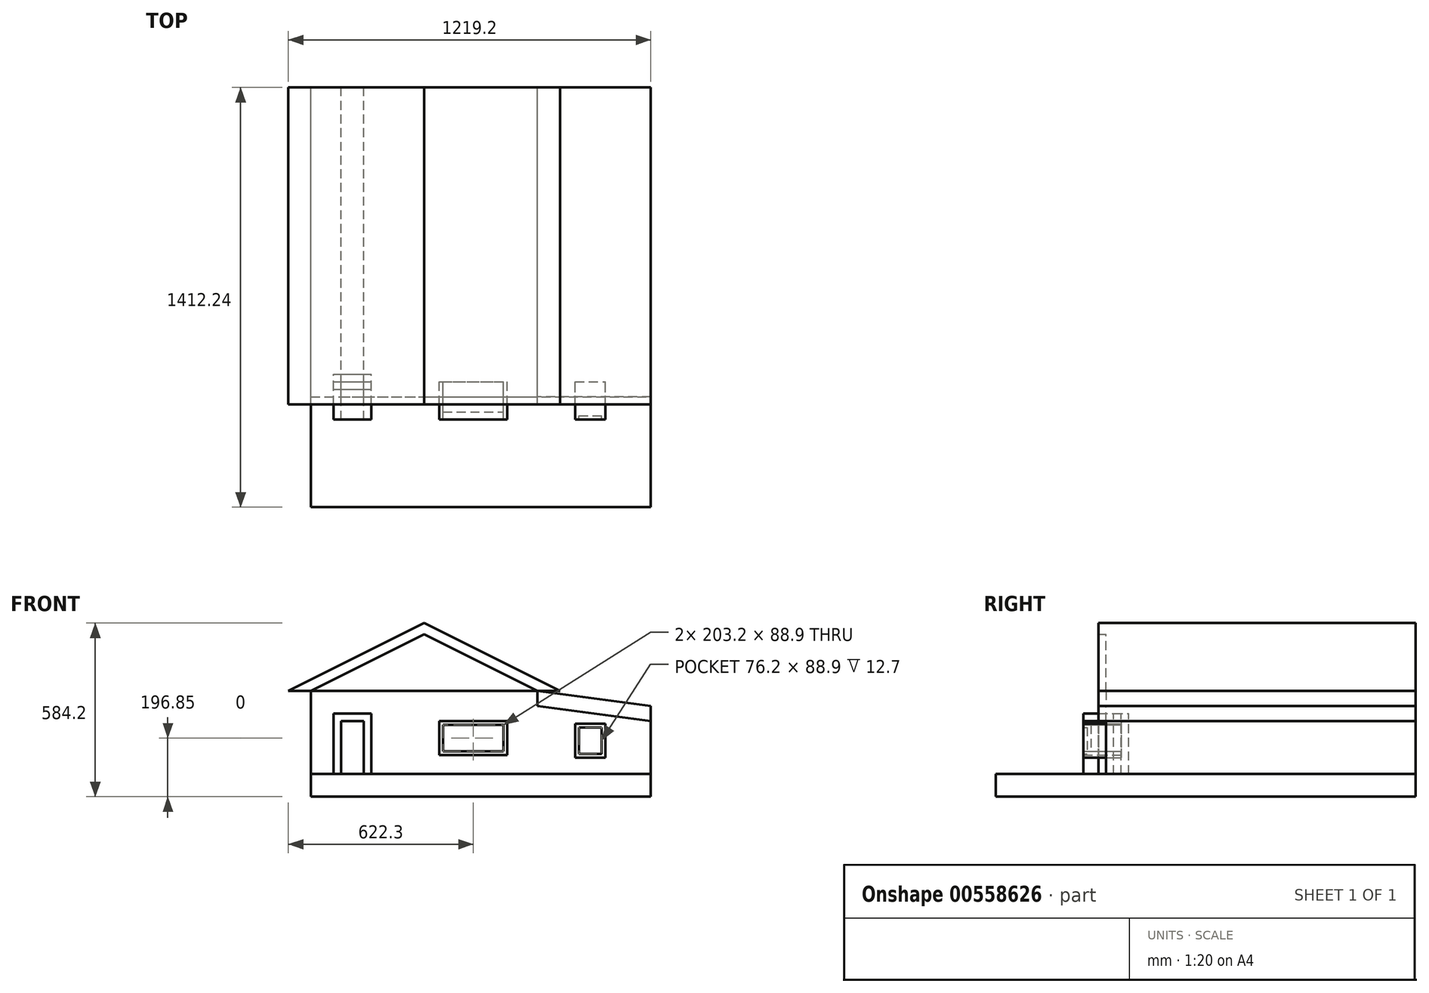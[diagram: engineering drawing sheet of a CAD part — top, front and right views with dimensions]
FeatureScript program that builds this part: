
annotation { "Feature Type Name" : "Feature", "Feature Type Description" : "" }
export const myFeature = defineFeature(function(context is Context, id is Id, definition is map)
    precondition{}
    {
        {
            var Q0;
            Q0=qCreatedBy(makeId("Front.planeOp"),FACE);
            var sketch = newSketch(context, id + "F0", { "sketchPlane" : qUnion([Q0])});
            skLineSegment(sketch, "E0", {"start": v(0, 0) * mm, "end": v(-381, 0) * mm});
            skLineSegment(sketch, "E1", {"start": v(0, 0) * mm, "end": v(381, 0) * mm});
            skLineSegment(sketch, "E2.bottom", {"start": v(-381, 0) * mm, "end": v(381, 0) * mm});
            skLineSegment(sketch, "E2.top", {"start": v(-381, -279.4) * mm, "end": v(381, -279.4) * mm});
            skLineSegment(sketch, "E2.left", {"start": v(-381, 0) * mm, "end": v(-381, -279.4) * mm});
            skLineSegment(sketch, "E2.right", {"start": v(381, 0) * mm, "end": v(381, -279.4) * mm});
            skLineSegment(sketch, "E3", {"start": v(-381, 0) * mm, "end": v(0, 190.5) * mm});
            skLineSegment(sketch, "E4", {"start": v(0, 0) * mm, "end": v(0, 190.5) * mm});
            skLineSegment(sketch, "E5", {"start": v(0, 190.5) * mm, "end": v(381, 0) * mm});
            skLineSegment(sketch, "E6", {"start": v(0, 190.5) * mm, "end": v(0, 228.6) * mm});
            skLineSegment(sketch, "E7", {"start": v(-381, 0) * mm, "end": v(-457.2, 0) * mm});
            skLineSegment(sketch, "E8", {"start": v(381, 0) * mm, "end": v(457.2, 0) * mm});
            skLineSegment(sketch, "E9", {"start": v(-457.2, 0) * mm, "end": v(0, 228.6) * mm});
            skLineSegment(sketch, "E10", {"start": v(0, 228.6) * mm, "end": v(457.2, 0) * mm});
            skLineSegment(sketch, "E11", {"start": v(-381, -279.4) * mm, "end": v(-381, -355.6) * mm});
            skLineSegment(sketch, "E12", {"start": v(-381, -355.6) * mm, "end": v(381, -355.6) * mm});
            skLineSegment(sketch, "E13", {"start": v(381, -279.4) * mm, "end": v(381, -355.6) * mm});
            skLineSegment(sketch, "E14", {"start": v(381, -279.4) * mm, "end": v(762, -279.4) * mm});
            skLineSegment(sketch, "E15", {"start": v(762, -279.4) * mm, "end": v(762, -355.6) * mm});
            skLineSegment(sketch, "E16", {"start": v(381, -355.6) * mm, "end": v(762, -355.6) * mm});
            skLineSegment(sketch, "E17", {"start": v(762, -279.4) * mm, "end": v(762, -50.8) * mm});
            skLineSegment(sketch, "E18", {"start": v(381, 0) * mm, "end": v(762, -50.8) * mm});
            skLineSegment(sketch, "E19", {"start": v(762, -50.8) * mm, "end": v(762, -101.6) * mm});
            skLineSegment(sketch, "E20", {"start": v(762, -101.6) * mm, "end": v(381, -50.8) * mm});
            skLineSegment(sketch, "E21.bottom", {"start": v(50.8, -101.6) * mm, "end": v(279.4, -101.6) * mm});
            skLineSegment(sketch, "E21.top", {"start": v(50.8, -215.9) * mm, "end": v(279.4, -215.9) * mm});
            skLineSegment(sketch, "E21.left", {"start": v(50.8, -101.6) * mm, "end": v(50.8, -215.9) * mm});
            skLineSegment(sketch, "E21.right", {"start": v(279.4, -101.6) * mm, "end": v(279.4, -215.9) * mm});
            skLineSegment(sketch, "E22.0", {"start": v(63.5, -114.3) * mm, "end": v(266.7, -114.3) * mm});
            skLineSegment(sketch, "E22.1", {"start": v(63.5, -114.3) * mm, "end": v(63.5, -203.2) * mm});
            skLineSegment(sketch, "E22.2", {"start": v(63.5, -203.2) * mm, "end": v(266.7, -203.2) * mm});
            skLineSegment(sketch, "E22.3", {"start": v(266.7, -114.3) * mm, "end": v(266.7, -203.2) * mm});
            skLineSegment(sketch, "E23.bottom", {"start": v(-279.4, -279.4) * mm, "end": v(-203.2, -279.4) * mm});
            skLineSegment(sketch, "E23.top", {"start": v(-279.4, -101.6) * mm, "end": v(-203.2, -101.6) * mm});
            skLineSegment(sketch, "E23.left", {"start": v(-279.4, -279.4) * mm, "end": v(-279.4, -101.6) * mm});
            skLineSegment(sketch, "E23.right", {"start": v(-203.2, -279.4) * mm, "end": v(-203.2, -101.6) * mm});
            skLineSegment(sketch, "E24.0", {"start": v(-177.8, -279.4) * mm, "end": v(-177.8, -76.2) * mm});
            skLineSegment(sketch, "E24.1", {"start": v(-304.8, -76.2) * mm, "end": v(-177.8, -76.2) * mm});
            skLineSegment(sketch, "E24.2", {"start": v(-304.8, -279.4) * mm, "end": v(-304.8, -76.2) * mm});
            skLineSegment(sketch, "E25", {"start": v(508, -109.47) * mm, "end": v(609.6, -109.47) * mm});
            skLineSegment(sketch, "E26", {"start": v(508, -109.47) * mm, "end": v(508, -223.77) * mm});
            skLineSegment(sketch, "E27", {"start": v(508, -223.77) * mm, "end": v(609.6, -223.77) * mm});
            skLineSegment(sketch, "E28", {"start": v(609.6, -109.47) * mm, "end": v(609.6, -223.77) * mm});
            skLineSegment(sketch, "E29.0", {"start": v(520.7, -122.17) * mm, "end": v(596.9, -122.17) * mm});
            skLineSegment(sketch, "E29.1", {"start": v(520.7, -122.17) * mm, "end": v(520.7, -211.07) * mm});
            skLineSegment(sketch, "E29.2", {"start": v(520.7, -211.07) * mm, "end": v(596.9, -211.07) * mm});
            skLineSegment(sketch, "E29.3", {"start": v(596.9, -122.17) * mm, "end": v(596.9, -211.07) * mm});
            skSolve(sketch);
        }
        {
            var Q0;
            Q0=makeQuery(id+"F0.imprint","IMPRINT",FACE,{"disambiguationData":[TD([[makeQuery(id+"F0.imprint","IMPRINT",EDGE,{"derivedFrom":sQuery(id+"F0.wireOp",EDGE,"E3")}),1.0]])]});
            var Q1;
            Q1=makeQuery(id+"F0.imprint","IMPRINT",FACE,{"disambiguationData":[TD([[makeQuery(id+"F0.imprint","IMPRINT",EDGE,{"derivedFrom":sQuery(id+"F0.wireOp",EDGE,"E5")}),1.0]])]});
            var Q2;
            {var subQ0=sQuery(id+"F0.wireOp",EDGE,"E18");Q2=makeQuery(id+"F0.imprint","IMPRINT",FACE,{"disambiguationData":[TD([[makeQuery(id+"F0.imprint","IMPRINT",EDGE,{"derivedFrom":subQ0}),-1.0]])]});}
            extrude(context, id + "F1", {"entities" : qUnion([Q0, Q1, Q2]), "depth" : 50.8 * mm, "offsetDistance" : 25.4 * mm, "hasSecondDirection" : true, "secondDirectionOppositeDirection" : true, "secondDirectionDepth" : 1016 * mm});
        }
        {
            var Q0;
            {var subQ2=sQuery(id+"F0.wireOp",EDGE,"E4");Q0=makeQuery(id+"F0.imprint","IMPRINT",FACE,{"disambiguationData":[TD([[makeQuery(id+"F0.imprint","IMPRINT",EDGE,{"derivedFrom":subQ2}),-1.0]])]});}
            var Q1;
            {var subQ0=sQuery(id+"F0.wireOp",EDGE,"E3");Q1=makeQuery(id+"F0.imprint","IMPRINT",FACE,{"disambiguationData":[TD([[makeQuery(id+"F0.imprint","IMPRINT",EDGE,{"derivedFrom":subQ0}),-1.0]])]});}
            extrude(context, id + "F2", {"entities" : qUnion([Q0, Q1]), "operationType" : NewBodyOperationType.ADD, "depth" : 25.4 * mm, "offsetDistance" : 25.4 * mm, "hasSecondDirection" : true, "secondDirectionOppositeDirection" : true, "secondDirectionDepth" : 1016 * mm});
        }
        {
            var Q0;
            Q0=makeQuery(id+"F0.imprint","IMPRINT",FACE,{"disambiguationData":[TD([[makeQuery(id+"F0.imprint","IMPRINT",EDGE,{"derivedFrom":sQuery(id+"F0.wireOp",EDGE,"E21.bottom")}),-1.0]])]});
            var Q1;
            Q1=makeQuery(id+"F0.imprint","IMPRINT",FACE,{"disambiguationData":[TD([[makeQuery(id+"F0.imprint","IMPRINT",EDGE,{"derivedFrom":sQuery(id+"F0.wireOp",EDGE,"E23.top")}),1.0]])]});
            var Q2;
            Q2=makeQuery(id+"F0.imprint","IMPRINT",FACE,{"disambiguationData":[TD([[makeQuery(id+"F0.imprint","IMPRINT",EDGE,{"derivedFrom":sQuery(id+"F0.wireOp",EDGE,"E25")}),-1.0]])]});
            extrude(context, id + "F3", {"entities" : qUnion([Q0, Q1, Q2]), "depth" : 50.8 * mm, "offsetDistance" : 25.4 * mm, "hasSecondDirection" : true, "secondDirectionOppositeDirection" : true, "secondDirectionDepth" : 25.4 * mm});
        }
        {
            var Q0;
            Q0=makeQuery(id+"F0.imprint","IMPRINT",FACE,{"disambiguationData":[TD([[makeQuery(id+"F0.imprint","IMPRINT",EDGE,{"derivedFrom":sQuery(id+"F0.wireOp",EDGE,"E22.0")}),-1.0]])]});
            var Q1;
            Q1=makeQuery(id+"F0.imprint","IMPRINT",FACE,{"disambiguationData":[TD([[makeQuery(id+"F0.imprint","IMPRINT",EDGE,{"derivedFrom":sQuery(id+"F0.wireOp",EDGE,"E23.bottom")}),1.0]])]});
            var Q2;
            Q2=makeQuery(id+"F3.opExtrude","CAP_FACE",FACE,{"disambiguationData":[OSD([sQuery(id+"F0.wireOp",EDGE,"E2.top"),sQuery(id+"F0.wireOp",EDGE,"E23.top"),sQuery(id+"F0.wireOp",EDGE,"E23.left"),sQuery(id+"F0.wireOp",EDGE,"E23.right"),sQuery(id+"F0.wireOp",EDGE,"E24.0"),sQuery(id+"F0.wireOp",EDGE,"E24.1"),sQuery(id+"F0.wireOp",EDGE,"E24.2")])],"isStart":true});
            extrude(context, id + "F4", {"entities" : qUnion([Q0, Q1, Q2]), "depth" : 25.4 * mm, "offsetDistance" : 25.4 * mm, "hasSecondDirection" : true, "secondDirectionOppositeDirection" : true, "secondDirectionDepth" : 25.4 * mm});
        }
        {
            var Q0;
            Q0=makeQuery(id+"F3.opExtrude","CAP_FACE",FACE,{"disambiguationData":[OSD([sQuery(id+"F0.wireOp",EDGE,"E2.top"),sQuery(id+"F0.wireOp",EDGE,"E23.top"),sQuery(id+"F0.wireOp",EDGE,"E23.left"),sQuery(id+"F0.wireOp",EDGE,"E23.right"),sQuery(id+"F0.wireOp",EDGE,"E24.0"),sQuery(id+"F0.wireOp",EDGE,"E24.1"),sQuery(id+"F0.wireOp",EDGE,"E24.2")])],"isStart":false});
            var Q1;
            Q1=makeQuery(id+"F4.opExtrude","CAP_FACE",FACE,{"disambiguationData":[OSD([sQuery(id+"F0.wireOp",EDGE,"E23.bottom"),sQuery(id+"F0.wireOp",EDGE,"E23.top"),sQuery(id+"F0.wireOp",EDGE,"E23.left"),sQuery(id+"F0.wireOp",EDGE,"E23.right")])],"isStart":false});
            var Q2;
            Q2=makeQuery(id+"F3.opExtrude","CAP_FACE",FACE,{"disambiguationData":[OSD([sQuery(id+"F0.wireOp",EDGE,"E21.bottom"),sQuery(id+"F0.wireOp",EDGE,"E21.top"),sQuery(id+"F0.wireOp",EDGE,"E21.left"),sQuery(id+"F0.wireOp",EDGE,"E21.right"),sQuery(id+"F0.wireOp",EDGE,"E22.0"),sQuery(id+"F0.wireOp",EDGE,"E22.1"),sQuery(id+"F0.wireOp",EDGE,"E22.2"),sQuery(id+"F0.wireOp",EDGE,"E22.3")])],"isStart":false});
            var Q3;
            Q3=makeQuery(id+"F4.opExtrude","CAP_FACE",FACE,{"disambiguationData":[OSD([sQuery(id+"F0.wireOp",EDGE,"E22.0"),sQuery(id+"F0.wireOp",EDGE,"E22.1"),sQuery(id+"F0.wireOp",EDGE,"E22.2"),sQuery(id+"F0.wireOp",EDGE,"E22.3")])],"isStart":false});
            var Q4;
            Q4=makeQuery(id+"F3.opExtrude","CAP_FACE",FACE,{"disambiguationData":[OSD([sQuery(id+"F0.wireOp",EDGE,"E25"),sQuery(id+"F0.wireOp",EDGE,"E26"),sQuery(id+"F0.wireOp",EDGE,"E27"),sQuery(id+"F0.wireOp",EDGE,"E28"),sQuery(id+"F0.wireOp",EDGE,"E29.0"),sQuery(id+"F0.wireOp",EDGE,"E29.1"),sQuery(id+"F0.wireOp",EDGE,"E29.2"),sQuery(id+"F0.wireOp",EDGE,"E29.3")])],"isStart":false});
            extrude(context, id + "F5", {"entities" : qUnion([Q0, Q1, Q2, Q3, Q4]), "depth" : 50.8 * mm, "offsetDistance" : 25.4 * mm});
        }
        {
            var Q0;
            Q0=makeQuery(id+"F0.imprint","IMPRINT",FACE,{"disambiguationData":[TD([[makeQuery(id+"F0.imprint","IMPRINT",EDGE,{"derivedFrom":sQuery(id+"F0.wireOp",EDGE,"E29.0")}),-1.0]])]});
            extrude(context, id + "F6", {"entities" : qUnion([Q0]), "operationType" : NewBodyOperationType.ADD, "depth" : 88.9 * mm, "offsetDistance" : 25.4 * mm, "hasSecondDirection" : true, "secondDirectionOppositeDirection" : true, "secondDirectionDepth" : 25.4 * mm});
        }
        {
            var Q0;
            {var subQ1=sQuery(id+"F0.wireOp",EDGE,"E14");Q0=makeQuery(id+"F0.imprint","IMPRINT",FACE,{"disambiguationData":[TD([[makeQuery(id+"F0.imprint","IMPRINT",EDGE,{"derivedFrom":subQ1}),1.0]])]});}
            var Q1;
            {var subQ4=sQuery(id+"F0.wireOp",EDGE,"E2.left");Q1=makeQuery(id+"F0.imprint","IMPRINT",FACE,{"disambiguationData":[TD([[makeQuery(id+"F0.imprint","IMPRINT",EDGE,{"derivedFrom":subQ4}),1.0]])]});}
            var Q2;
            Q2=makeQuery(id+"F0.imprint","IMPRINT",FACE,{"disambiguationData":[TD([[makeQuery(id+"F0.imprint","IMPRINT",EDGE,{"derivedFrom":sQuery(id+"F0.wireOp",EDGE,"E23.bottom")}),1.0]])]});
            var Q3;
            Q3=makeQuery(id+"F0.imprint","IMPRINT",FACE,{"disambiguationData":[TD([[makeQuery(id+"F0.imprint","IMPRINT",EDGE,{"derivedFrom":sQuery(id+"F0.wireOp",EDGE,"E22.0")}),-1.0]])]});
            var Q4;
            Q4=makeQuery(id+"F0.imprint","IMPRINT",FACE,{"disambiguationData":[TD([[makeQuery(id+"F0.imprint","IMPRINT",EDGE,{"derivedFrom":sQuery(id+"F0.wireOp",EDGE,"E29.0")}),-1.0]])]});
            var Q5;
            Q5=makeQuery(id+"F0.imprint","IMPRINT",FACE,{"disambiguationData":[TD([[makeQuery(id+"F0.imprint","IMPRINT",EDGE,{"derivedFrom":sQuery(id+"F0.wireOp",EDGE,"E25")}),-1.0]])]});
            var Q6;
            Q6=makeQuery(id+"F0.imprint","IMPRINT",FACE,{"disambiguationData":[TD([[makeQuery(id+"F0.imprint","IMPRINT",EDGE,{"derivedFrom":sQuery(id+"F0.wireOp",EDGE,"E21.bottom")}),-1.0]])]});
            var Q7;
            Q7=makeQuery(id+"F0.imprint","IMPRINT",FACE,{"disambiguationData":[TD([[makeQuery(id+"F0.imprint","IMPRINT",EDGE,{"derivedFrom":sQuery(id+"F0.wireOp",EDGE,"E23.top")}),1.0]])]});
            extrude(context, id + "F7", {"entities" : qUnion([Q0, Q1, Q2, Q3, Q4, Q5, Q6, Q7]), "depth" : 25.4 * mm, "offsetDistance" : 25.4 * mm, "hasSecondDirection" : true, "secondDirectionOppositeDirection" : true, "secondDirectionDepth" : 1016 * mm});
        }
        {
            var Q0;
            {var subQ5=sQuery(id+"F0.wireOp",EDGE,"E11");Q0=makeQuery(id+"F0.imprint","IMPRINT",FACE,{"disambiguationData":[TD([[makeQuery(id+"F0.imprint","IMPRINT",EDGE,{"derivedFrom":subQ5}),1.0]])]});}
            var Q1;
            Q1=makeQuery(id+"F0.imprint","IMPRINT",FACE,{"disambiguationData":[TD([[makeQuery(id+"F0.imprint","IMPRINT",EDGE,{"derivedFrom":sQuery(id+"F0.wireOp",EDGE,"E13")}),1.0]])]});
            extrude(context, id + "F8", {"entities" : qUnion([Q0, Q1]), "depth" : 396.24 * mm, "offsetDistance" : 25.4 * mm, "hasSecondDirection" : true, "secondDirectionOppositeDirection" : true, "secondDirectionDepth" : 1016 * mm});
        }
    });
